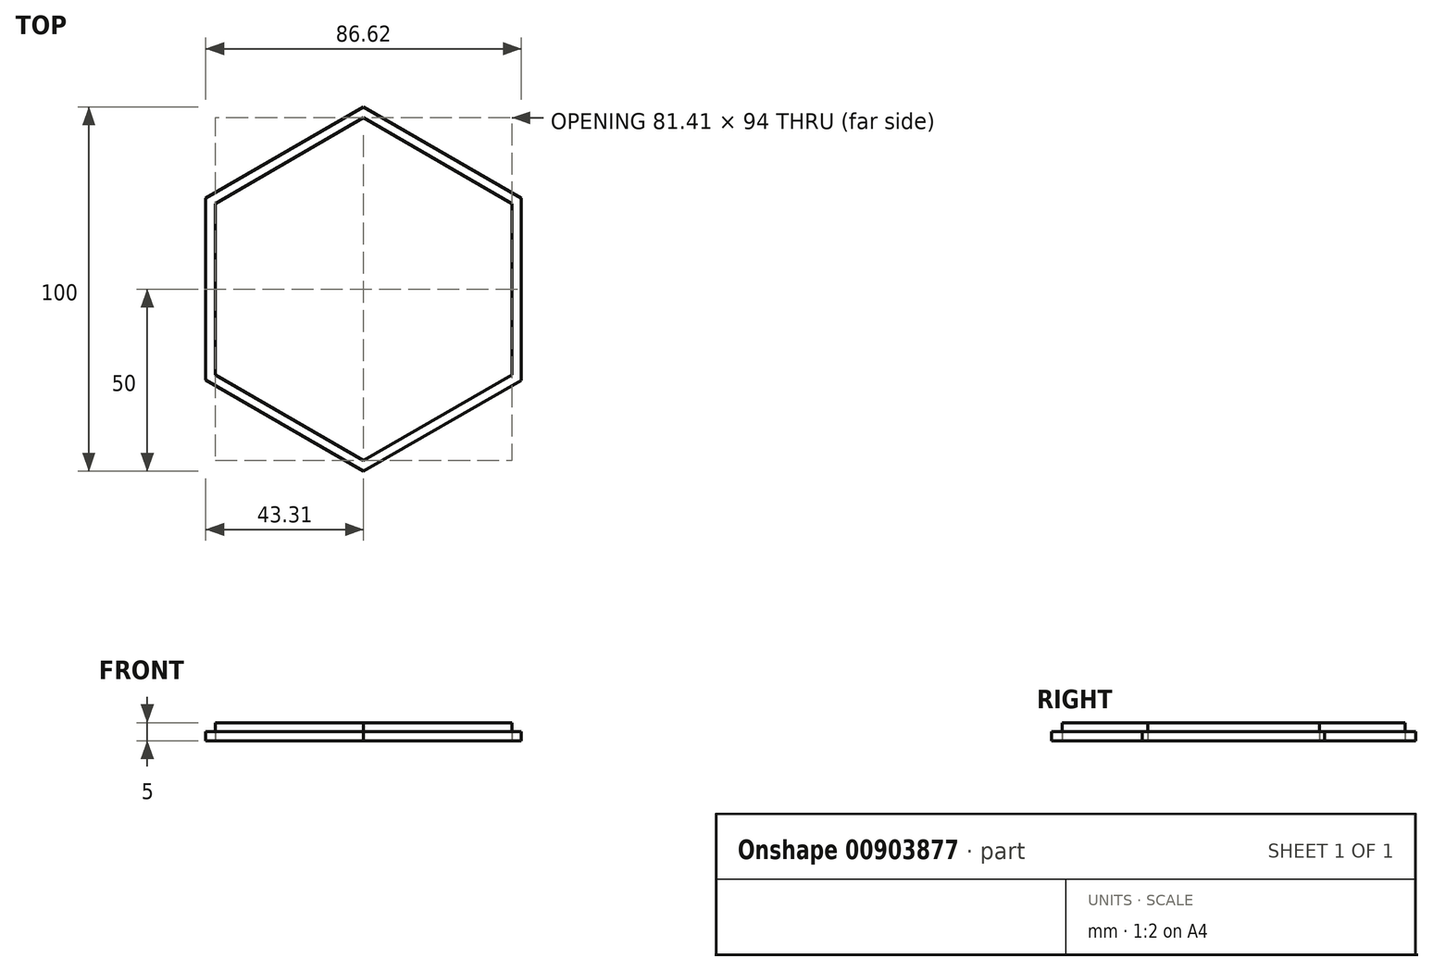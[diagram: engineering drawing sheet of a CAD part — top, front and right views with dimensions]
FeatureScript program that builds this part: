
annotation { "Feature Type Name" : "Feature", "Feature Type Description" : "" }
export const myFeature = defineFeature(function(context is Context, id is Id, definition is map)
    precondition{}
    {
        {
            var Q0;
            Q0=qCreatedBy(makeId("Top.planeOp"),FACE);
            var sketch = newSketch(context, id + "F0", { "sketchPlane" : qUnion([Q0])});
            skCircle(sketch, "E0.cCircle", {"center": v(0, 0) * mm, "radius": 43.3 * mm, "construction": true});
            skLineSegment(sketch, "E0.0", {"start": v(-0.02, -50) * mm, "end": v(-43.31, -24.98) * mm});
            skLineSegment(sketch, "E0.1", {"start": v(-43.31, -24.98) * mm, "end": v(-43.29, 25.02) * mm});
            skLineSegment(sketch, "E0.2", {"start": v(-43.29, 25.02) * mm, "end": v(0.02, 50) * mm});
            skLineSegment(sketch, "E0.3", {"start": v(0.02, 50) * mm, "end": v(43.31, 24.98) * mm});
            skLineSegment(sketch, "E0.4", {"start": v(43.31, 24.98) * mm, "end": v(43.29, -25.02) * mm});
            skLineSegment(sketch, "E0.5", {"start": v(43.29, -25.02) * mm, "end": v(-0.02, -50) * mm});
            skPoint(sketch, "E0.0.midPoint", {"position": v(-21.67, -37.49) * mm});
            skCircle(sketch, "E1.cCircle", {"center": v(0, 0) * mm, "radius": 40.7 * mm, "construction": true});
            skLineSegment(sketch, "E1.0", {"start": v(-40.7, -23.5) * mm, "end": v(-40.7, 23.5) * mm});
            skLineSegment(sketch, "E1.1", {"start": v(-40.7, 23.5) * mm, "end": v(0, 47) * mm});
            skLineSegment(sketch, "E1.2", {"start": v(0, 47) * mm, "end": v(40.7, 23.5) * mm});
            skLineSegment(sketch, "E1.3", {"start": v(40.7, 23.5) * mm, "end": v(40.7, -23.5) * mm});
            skLineSegment(sketch, "E1.4", {"start": v(40.7, -23.5) * mm, "end": v(0, -47) * mm});
            skLineSegment(sketch, "E1.5", {"start": v(0, -47) * mm, "end": v(-40.7, -23.5) * mm});
            skPoint(sketch, "E1.0.midPoint", {"position": v(-40.7, 0) * mm});
            skSolve(sketch);
        }
        {
            var Q0;
            Q0=makeQuery(id+"F0.imprint","IMPRINT",FACE,{"disambiguationData":[TD([[makeQuery(id+"F0.imprint","IMPRINT",EDGE,{"derivedFrom":sQuery(id+"F0.wireOp",EDGE,"E0.0")}),-1.0]])]});
            extrude(context, id + "F1", {"entities" : qUnion([Q0]), "depth" : 2.5 * mm, "offsetDistance" : 25 * mm});
        }
        {
            var Q0;
            Q0=makeQuery(id+"F0.imprint","IMPRINT",FACE,{"disambiguationData":[TD([[makeQuery(id+"F0.imprint","IMPRINT",EDGE,{"derivedFrom":sQuery(id+"F0.wireOp",EDGE,"E1.0")}),-1.0]])]});
            extrude(context, id + "F2", {"entities" : qUnion([Q0]), "depth" : 5 * mm, "offsetDistance" : 25 * mm});
        }
    });
